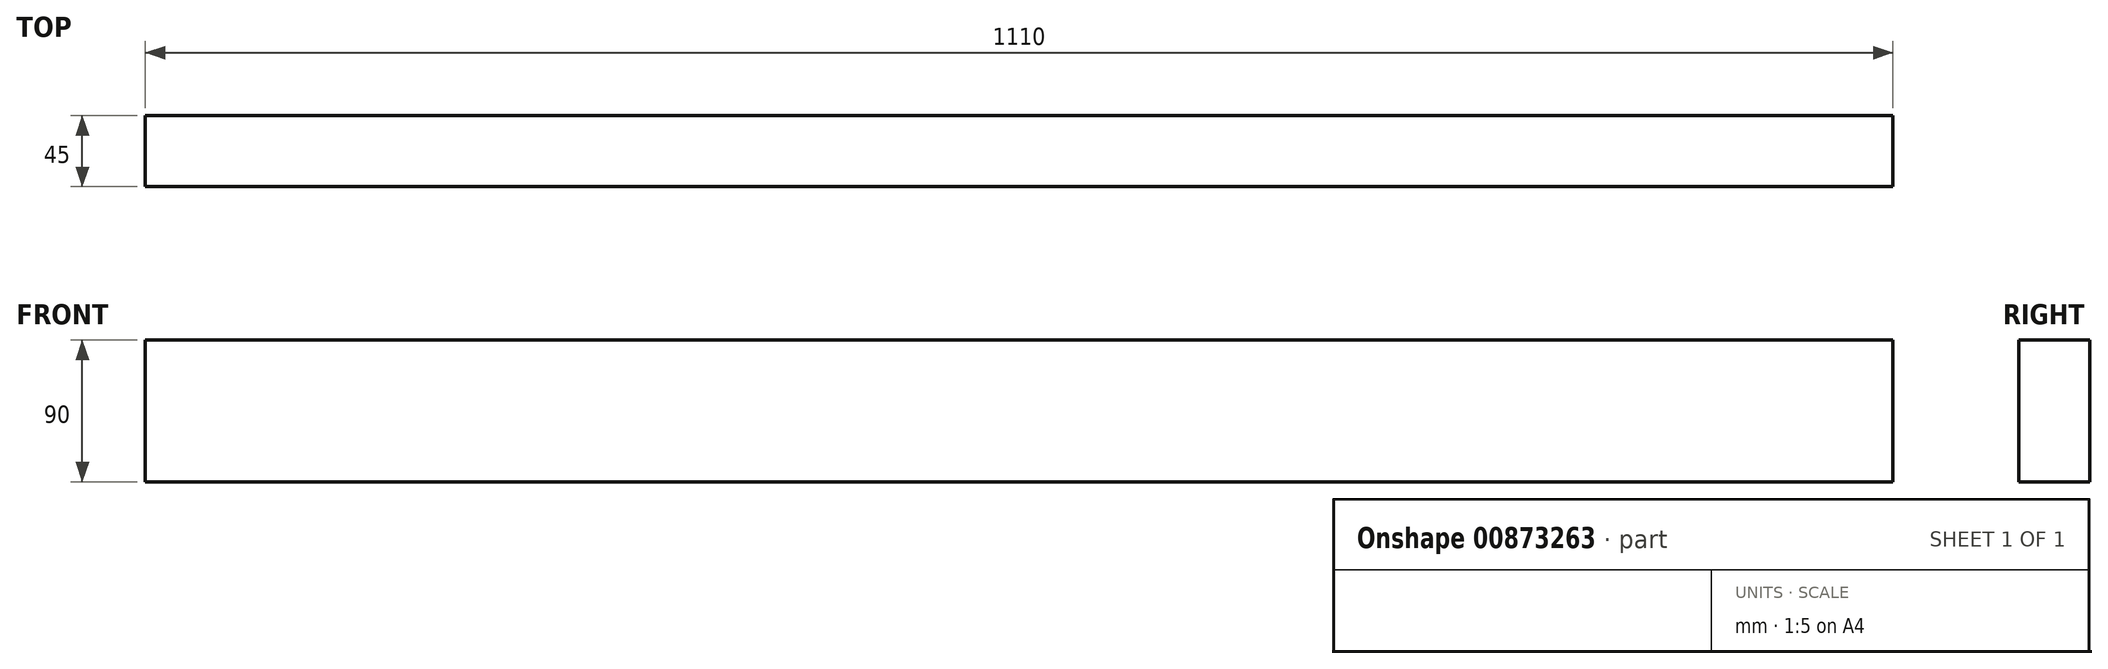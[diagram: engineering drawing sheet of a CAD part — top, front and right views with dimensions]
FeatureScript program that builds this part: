
annotation { "Feature Type Name" : "Feature", "Feature Type Description" : "" }
export const myFeature = defineFeature(function(context is Context, id is Id, definition is map)
    precondition{}
    {
        {
            var Q0;
            Q0=qCreatedBy(makeId("Front.planeOp"),FACE);
            var sketch = newSketch(context, id + "F0", { "sketchPlane" : qUnion([Q0])});
            skLineSegment(sketch, "E0.bottom", {"start": v(-555, 45) * mm, "end": v(555, 45) * mm});
            skLineSegment(sketch, "E0.top", {"start": v(-555, -45) * mm, "end": v(555, -45) * mm});
            skLineSegment(sketch, "E0.left", {"start": v(-555, 45) * mm, "end": v(-555, -45) * mm});
            skLineSegment(sketch, "E0.right", {"start": v(555, 45) * mm, "end": v(555, -45) * mm});
            skPoint(sketch, "E0.middle", {"position": v(0, 0) * mm});
            skSolve(sketch);
        }
        {
            var Q0;
            Q0 = qSketchRegion(id + "F0", true);
            extrude(context, id + "F1", {"entities" : qUnion([Q0]), "depth" : 45 * mm, "offsetDistance" : 25 * mm});
        }
    });
